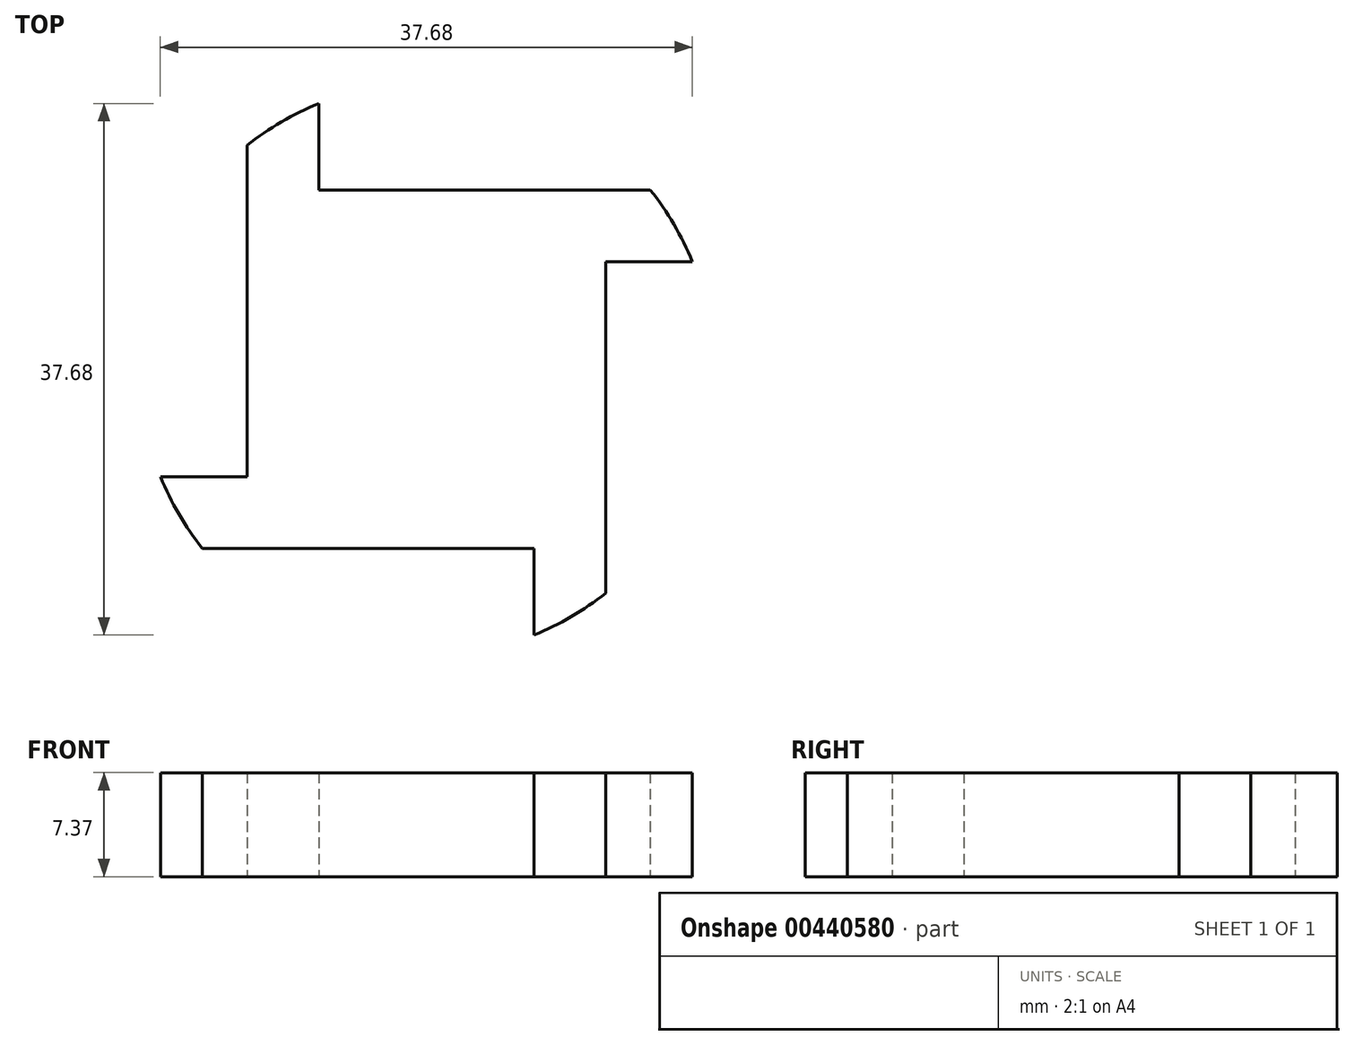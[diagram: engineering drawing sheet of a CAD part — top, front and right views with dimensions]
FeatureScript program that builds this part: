
annotation { "Feature Type Name" : "Feature", "Feature Type Description" : "" }
export const myFeature = defineFeature(function(context is Context, id is Id, definition is map)
    precondition{}
    {
        {
            var Q0;
            Q0=qCreatedBy(makeId("Top.planeOp"),FACE);
            var sketch = newSketch(context, id + "F0", { "sketchPlane" : qUnion([Q0])});
            skLineSegment(sketch, "E0.bottom", {"start": v(0, 0) * mm, "end": v(25.4, 0) * mm});
            skLineSegment(sketch, "E0.top", {"start": v(0, 25.4) * mm, "end": v(25.4, 25.4) * mm});
            skLineSegment(sketch, "E0.left", {"start": v(0, 0) * mm, "end": v(0, 25.4) * mm});
            skLineSegment(sketch, "E0.right", {"start": v(25.4, 0) * mm, "end": v(25.4, 25.4) * mm});
            skSolve(sketch);
        }
        {
            var Q0;
            Q0 = qSketchRegion(id + "F0", true);
            extrude(context, id + "F1", {"entities" : qUnion([Q0]), "depth" : 7.37 * mm});
        }
        {
            var Q0;
            Q0=qCreatedBy(makeId("Top.planeOp"),FACE);
            var sketch = newSketch(context, id + "F2", { "sketchPlane" : qUnion([Q0])});
            skLineSegment(sketch, "E1", {"start": v(0, 0) * mm, "end": v(25.4, 25.4) * mm, "construction": true});
            skArc(sketch, "E2", {"start": v(5.08, 31.54) * mm, "mid": v(2.43, 30.23) * mm, "end": v(0, 28.56) * mm});
            skLineSegment(sketch, "E3", {"start": v(0, 25.4) * mm, "end": v(0, 28.56) * mm});
            skLineSegment(sketch, "E4", {"start": v(5.08, 25.4) * mm, "end": v(5.08, 31.54) * mm});
            skLineSegment(sketch, "E5", {"start": v(0, 25.4) * mm, "end": v(5.08, 25.4) * mm});
            skLineSegment(sketch, "E6", {"start": v(25.4, 25.4) * mm, "end": v(28.56, 25.4) * mm});
            skLineSegment(sketch, "E7", {"start": v(0, 0) * mm, "end": v(-3.16, 0) * mm});
            skLineSegment(sketch, "E8", {"start": v(25.4, 0) * mm, "end": v(25.4, -3.16) * mm});
            skLineSegment(sketch, "E9", {"start": v(31.54, 20.32) * mm, "end": v(25.4, 20.32) * mm});
            skLineSegment(sketch, "E10", {"start": v(25.4, 25.4) * mm, "end": v(25.4, 20.32) * mm});
            skLineSegment(sketch, "E11", {"start": v(20.32, -6.14) * mm, "end": v(20.32, 0) * mm});
            skLineSegment(sketch, "E12", {"start": v(-6.14, 5.08) * mm, "end": v(0, 5.08) * mm});
            skLineSegment(sketch, "E13", {"start": v(0, 0) * mm, "end": v(0, 5.08) * mm});
            skLineSegment(sketch, "E14", {"start": v(25.4, 0) * mm, "end": v(20.32, 0) * mm});
            skPoint(sketch, "E15.orphan", {"position": v(20.32, 2.55) * mm});
            skPoint(sketch, "E16.orphan", {"position": v(2.7, 5.08) * mm});
            skArc(sketch, "E17.trimOffspring", {"start": v(31.54, 20.32) * mm, "mid": v(30.23, 22.97) * mm, "end": v(28.56, 25.4) * mm});
            skArc(sketch, "E18.trimOffspring", {"start": v(20.32, -6.14) * mm, "mid": v(22.97, -4.83) * mm, "end": v(25.4, -3.16) * mm});
            skArc(sketch, "E19.trimOffspring", {"start": v(-6.14, 5.08) * mm, "mid": v(-4.83, 2.43) * mm, "end": v(-3.16, 0) * mm});
            skSolve(sketch);
        }
        {
            var Q0;
            Q0=makeQuery(id+"F2.imprint","IMPRINT",FACE,{"disambiguationData":[TD([[makeQuery(id+"F2.imprint","IMPRINT",EDGE,{"derivedFrom":sQuery(id+"F2.wireOp",EDGE,"E2")}),1.0]])]});
            var Q1;
            Q1=makeQuery(id+"F2.imprint","IMPRINT",FACE,{"disambiguationData":[TD([[makeQuery(id+"F2.imprint","IMPRINT",EDGE,{"derivedFrom":sQuery(id+"F2.wireOp",EDGE,"E6")}),-1.0]])]});
            var Q2;
            Q2=makeQuery(id+"F2.imprint","IMPRINT",FACE,{"disambiguationData":[TD([[makeQuery(id+"F2.imprint","IMPRINT",EDGE,{"derivedFrom":sQuery(id+"F2.wireOp",EDGE,"E8")}),-1.0]])]});
            var Q3;
            Q3=makeQuery(id+"F2.imprint","IMPRINT",FACE,{"disambiguationData":[TD([[makeQuery(id+"F2.imprint","IMPRINT",EDGE,{"derivedFrom":sQuery(id+"F2.wireOp",EDGE,"E7")}),-1.0]])]});
            extrude(context, id + "F3", {"entities" : qUnion([Q0, Q1, Q2, Q3]), "operationType" : NewBodyOperationType.ADD, "depth" : 7.37 * mm});
        }
    });
